# Revit family: Storage-Vessel_AO_Smith-ST-600_N_E
name_source: partatom
category: Mechanical Equipment
revit_build: Autodesk Revit 2016 (Build: 20170117_1200(x64)
units: mm (PartAtom-declared; Revit-internal decimal feet)

## family parameters
Always vertical = Yes
Cut with Voids When Loaded = No
OmniClass Number = 23.75.00.00
OmniClass Title = Climate Control (HVAC)
Part Type = Normal
Room Calculation Point = No
Round Connector Dimension = Use Radius
Shared = No
Work Plane-Based = No

## types (1)
- Storage-Vessel_AO_Smith-ST-600_N_E
    1e Maintenance (check-up) = 3 maanden na installatie
    2nd Maintenance (general maintenance) = 12 maanden na installatie
    Assembly Code = D3010
    BIM Content Developer = CAD & Company
    BIM Content Developer URL = http:/www.cadcompany.nl
    Cold Water Connection R = 1 1/2"
    Description = Voorraadvat
    Destination / Counrty = Nederland
    Diameter (with insulation) = 910 mm  [stored 2.98556 ft]
    Diameter (without insulation) = 750 mm  [stored 2.46063 ft]
    Empty Weight = 179.00 kg
    Height (with insulation) = 1840 mm  [stored 6.03675 ft]
    Height (without insulation) = 1805 mm  [stored 5.92192 ft]
    Height Cold Water Inlet = 85 mm  [stored 0.278871 ft]
    Height Warm Water Outlet = 1805 mm  [stored 5.92192 ft]
    Hot / Warm Water Connection R = 1 1/2"
    Insulation Thickness = 80 mm  [stored 0.262467 ft]
    Maintenance Interval = 12 maanden
    Manufacturer = A.O. Smith Water Products Company b.v.
    Manufacturer Number = E 7110
E 7110
E 7110
    Max. Operating Pressure - tank = 1000000.0 Pa
    Max. Temperature - tank = 95 °C
    Model = ST 600 N E
    Operating Weight = 857.00 kg
    Packaging Height = 1930 mm
    Packaging Length = 870 mm
    Packaging Width = 870 mm
    Product Documentation Link = https://www.aosmithinternational.com
    Product Instruction Link = https://www.aosmithinternational.com
    Serial Number = 8717449179977
    Storage Capacity - tank = 678 m³
    T&P Connection Rp = 1"
    Transport Weight = 251.00 kg
    Type of Packaging = Plastic en Hout
    URL = www.aosmith.nl
    Warranty on Parts = 12 maanden
    Warranty on Tank = 36 maanden
    Workspace Diameter = 1910 mm  [stored 6.2664 ft]
    Workspace Height = 2840 mm

note: [stored X ft] marks values corroborated as IEEE doubles in the binary element streams (Revit-internal decimal feet)

## geometry (parser evidence)
native form markers: Blend x4, Sweep x15
no freeform markers — native parametric forms only
